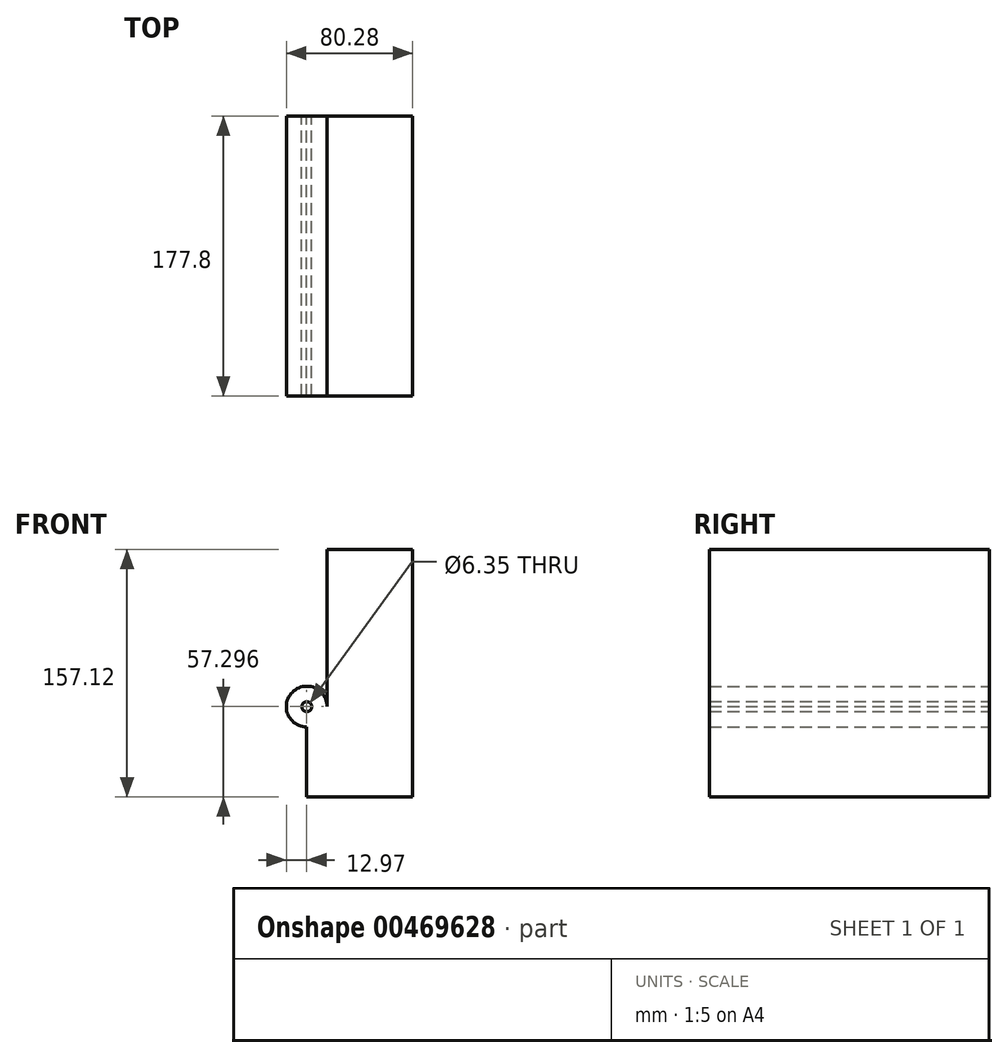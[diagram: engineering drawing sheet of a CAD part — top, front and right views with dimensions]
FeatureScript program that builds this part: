
annotation { "Feature Type Name" : "Feature", "Feature Type Description" : "" }
export const myFeature = defineFeature(function(context is Context, id is Id, definition is map)
    precondition{}
    {
        {
            var Q0;
            Q0=qCreatedBy(makeId("Front.planeOp"),FACE);
            var sketch = newSketch(context, id + "F0", { "sketchPlane" : qUnion([Q0])});
            skLineSegment(sketch, "E0.bottom", {"start": v(-35.23, 21.05) * mm, "end": v(32.08, 21.05) * mm});
            skLineSegment(sketch, "E0.top", {"start": v(-35.23, -36.25) * mm, "end": v(32.08, -36.25) * mm});
            skLineSegment(sketch, "E0.left", {"start": v(-35.23, 21.05) * mm, "end": v(-35.23, -36.25) * mm});
            skLineSegment(sketch, "E0.right", {"start": v(32.08, 21.05) * mm, "end": v(32.08, -36.25) * mm});
            skCircle(sketch, "E1", {"center": v(-35.23, 21.05) * mm, "radius": 12.97 * mm});
            skSolve(sketch);
        }
        {
            var Q0;
            {var subQ2=sQuery(id+"F0.wireOp",EDGE,"E0.top");Q0=makeQuery(id+"F0.imprint","IMPRINT",FACE,{"disambiguationData":[TD([[makeQuery(id+"F0.imprint","IMPRINT",EDGE,{"derivedFrom":subQ2}),1.0]])]});}
            var Q1;
            {var subQ0=sQuery(id+"F0.wireOp",EDGE,"E0.left");var subQ1=sQuery(id+"F0.wireOp",EDGE,"E0.bottom");var subQ2=makeQuery(id+"F0.imprint","INTERSECT",VERTEX,{"derivedFrom":[subQ1,subQ0]});Q1=makeQuery(id+"F0.imprint","IMPRINT",FACE,{"disambiguationData":[TD([[makeQuery(id+"F0.imprint","IMPRINT",EDGE,{"disambiguationData":[TD([[subQ2,-1.0]])],"derivedFrom":subQ1}),-1.0]])]});}
            var Q2;
            {var subQ0=sQuery(id+"F0.wireOp",EDGE,"E0.left");var subQ1=sQuery(id+"F0.wireOp",EDGE,"E0.bottom");var subQ2=makeQuery(id+"F0.imprint","INTERSECT",VERTEX,{"derivedFrom":[subQ1,subQ0]});Q2=makeQuery(id+"F0.imprint","IMPRINT",FACE,{"disambiguationData":[TD([[makeQuery(id+"F0.imprint","IMPRINT",EDGE,{"disambiguationData":[TD([[subQ2,-1.0]])],"derivedFrom":subQ1}),1.0]])]});}
            extrude(context, id + "F1", {"entities" : qUnion([Q0, Q1, Q2]), "depth" : 25.4 * mm});
        }
        {
            var Q0;
            Q0 = qSketchRegion(id + "F9UJlheGOLTi5Xn_1", true);
            var Q1;
            Q1=makeQuery(id+"F1.opExtrude","CAP_FACE",FACE,{"disambiguationData":[OSD([sQuery(id+"F0.wireOp",EDGE,"E0.bottom"),sQuery(id+"F0.wireOp",EDGE,"E0.top"),sQuery(id+"F0.wireOp",EDGE,"E0.left"),sQuery(id+"F0.wireOp",EDGE,"E0.right"),sQuery(id+"F0.wireOp",EDGE,"E1")])],"isStart":false});
            extrude(context, id + "F2", {"entities" : qUnion([Q0, Q1]), "operationType" : NewBodyOperationType.ADD, "depth" : 25.4 * mm});
        }
        {
            var Q0;
            {var subQ0=sQuery(id+"F0.wireOp",EDGE,"E0.bottom");Q0=makeQuery(id+"F2.boolean.opBoolean","MERGE",FACE,{"derivedFrom":[makeQuery(id+"F1.opExtrude","SWEPT_FACE",FACE,{"disambiguationData":[OSD([subQ0])]}),makeQuery(id+"F2.opExtrude","SWEPT_FACE",FACE,{"disambiguationData":[OSD([subQ0])]})]});}
            extrude(context, id + "F3", {"entities" : qUnion([Q0]), "operationType" : NewBodyOperationType.ADD, "depth" : 99.82 * mm, "hasSecondDirection" : true, "secondDirectionOppositeDirection" : true, "secondDirectionDepth" : 25.4 * mm});
        }
        {
            var Q0;
            Q0=sQuery(id+"F0.wireOp",VERTEX,"E1.center");
            var Q1;
            Q1=makeQuery(id+"F1.opExtrude","SWEPT_BODY",BODY,{"disambiguationData":[OSD([sQuery(id+"F0.wireOp",EDGE,"E0.bottom"),sQuery(id+"F0.wireOp",EDGE,"E0.top"),sQuery(id+"F0.wireOp",EDGE,"E0.left"),sQuery(id+"F0.wireOp",EDGE,"E0.right"),sQuery(id+"F0.wireOp",EDGE,"E1")])]});
            hole(context, id + "F4", {"style" : HoleStyle.SIMPLE, "endStyle" : HoleEndStyle.THROUGH, "oppositeDirection" : true, "holeDiameter" : 6.35 * mm, "isTappedThrough" : true, "tappedDepth" : 12.7 * mm, "tapClearance" : 3, "locations" : qUnion([Q0]), "scope" : qUnion([Q1])});
        }
        {
            var Q0;
            {var subQ0=sQuery(id+"F0.wireOp",EDGE,"E0.bottom");Q0=makeQuery(id+"F3.boolean.opBoolean","MERGE",FACE,{"derivedFrom":[makeQuery(id+"F1.opExtrude","CAP_FACE",FACE,{"disambiguationData":[OSD([subQ0,sQuery(id+"F0.wireOp",EDGE,"E0.top"),sQuery(id+"F0.wireOp",EDGE,"E0.left"),sQuery(id+"F0.wireOp",EDGE,"E0.right"),sQuery(id+"F0.wireOp",EDGE,"E1")])],"isStart":true}),makeQuery(id+"F3.opExtrude","SWEPT_FACE",FACE,{"disambiguationData":[OSD([subQ0]),TDD([makeQuery(id+"F1.opExtrude","CAP_EDGE",EDGE,{"disambiguationData":[OSD([subQ0])],"isStart":true})])]})]});}
            extrude(context, id + "F5", {"entities" : qUnion([Q0]), "operationType" : NewBodyOperationType.ADD, "depth" : 127 * mm});
        }
    });
